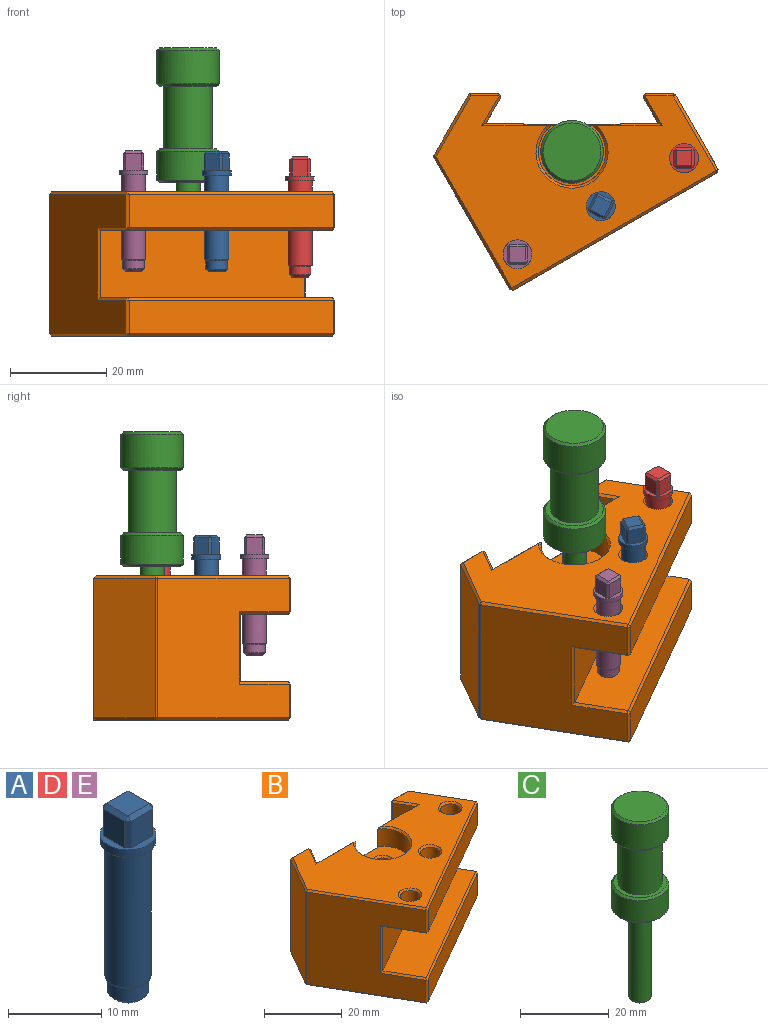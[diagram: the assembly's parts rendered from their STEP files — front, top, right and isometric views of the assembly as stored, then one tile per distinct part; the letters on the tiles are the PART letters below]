
ASSEMBLY  parts=5 mates=4
PART A: 25 faces, bbox 6x6x25 mm
  f0: cylinder r=3mm len=6mm, axis (0,0,-1), area 18.8mm2, adj f3,f5
  f1: cylinder r=2.25mm len=4.5mm, axis (0,0,-1), area 24.7mm2, adj f23,f24
  f2: plane 3.5x3.5mm, normal (0,0,-1), area 9.6mm2, adj f23
  f3: plane 6x6mm, normal (0,0,-1), area 8.6mm2, adj f0,f4
  f4: cylinder r=2.5mm len=17.5mm, axis (0,0,-1), area 274.9mm2, adj f3,f24
  f5: plane 6x6mm, normal (0,0,1), area 10.8mm2, adj f0,f6,f7,f8,f9,f11,f13,f16
  f6: plane 3.5x3.24mm, normal (0,1,0), area 11.3mm2, adj f5,f13,f19,f22
  f7: plane 3.5x3.24mm, normal (1,0,0), area 11.3mm2, adj f5,f11,f13,f14
  f8: plane 3.5x3.24mm, normal (0,-1,0), area 11.3mm2, adj f5,f11,f15,f16
  f9: plane 3.5x3.24mm, normal (-1,0,0), area 11.3mm2, adj f5,f16,f20,f22
  f10: plane 3.24x3.24mm, normal (0,0,1), area 10.5mm2, adj f14,f15,f19,f20
  f11: plane 3.5x0.5mm, normal (0.71,-0.71,0), area 2.5mm2, adj f5,f7,f8,f12
  f12: plane 0.5x0.5mm, normal (0.58,-0.58,0.58), area 0.2mm2, adj f11,f14,f15
  f13: plane 3.5x0.5mm, normal (0.71,0.71,0), area 2.5mm2, adj f5,f6,f7,f17
  f14: plane 3.24x0.5mm, normal (0.71,0,0.71), area 2.3mm2, adj f7,f10,f12,f17
  f15: plane 3.24x0.5mm, normal (0,-0.71,0.71), area 2.3mm2, adj f8,f10,f12,f18
  f16: plane 3.5x0.5mm, normal (-0.71,-0.71,0), area 2.5mm2, adj f5,f8,f9,f18
  f17: plane 0.5x0.5mm, normal (0.58,0.58,0.58), area 0.2mm2, adj f13,f14,f19
  f18: plane 0.5x0.5mm, normal (-0.58,-0.58,0.58), area 0.2mm2, adj f15,f16,f20
  f19: plane 3.24x0.5mm, normal (0,0.71,0.71), area 2.3mm2, adj f6,f10,f17,f21
  f20: plane 3.24x0.5mm, normal (-0.71,0,0.71), area 2.3mm2, adj f9,f10,f18,f21
  f21: plane 0.5x0.5mm, normal (-0.58,0.58,0.58), area 0.2mm2, adj f19,f20,f22
  f22: plane 3.5x0.5mm, normal (-0.71,0.71,0), area 2.5mm2, adj f5,f6,f9,f21
  f23: cone r=1.75mm half-angle=45deg, axis (0,0,1), area 8.9mm2, adj f1,f2
  f24: cone r=2mm half-angle=45deg, axis (0,0,1), area 5.3mm2, adj f1,f4
PART B: 83 faces, bbox 59.1x40.9x30 mm
  f0: plane 29x7.91mm, normal (0,1,0), area 229.4mm2, adj f3,f4,f13,f80
  f1: cylinder r=7mm len=14mm, axis (0,0,1), area 196.3mm2, adj f2,f5,f21,f82
  f2: cone r=7mm half-angle=45deg, axis (0,0,1), area 25.4mm2, adj f1,f3,f19,f38,f82
  f3: plane 14.51x0.5mm, normal (0,0.71,0.71), area 8.2mm2, adj f0,f2,f19,f56,f80,f82
  f4: plane 37.56x0.5mm, normal (0,0.71,-0.71), area 20.3mm2, adj f0,f10,f20,f55,f65,f80,f81,f82
  f5: plane 8.67x0.31mm, normal (0,0.71,0.71), area 3.5mm2, adj f1,f21,f82
  f6: plane 42.44x24.5mm, normal (0.5,-0.87,0), area 343mm2, adj f31,f32,f45,f46
  f7: cylinder r=2.5mm len=7mm, axis (0,0,1), area 110mm2, adj f73,f74
  f8: cylinder r=2.5mm len=7mm, axis (0,0,1), area 110mm2, adj f75,f76
  f9: cylinder r=2.5mm len=7mm, axis (0,0,1), area 110mm2, adj f77,f78
  f10: plane 29x7.91mm, normal (0,1,0), area 229.4mm2, adj f4,f12,f38,f81
  f11: plane 29.5x5.81mm, normal (0,1,0), area 171.3mm2, adj f20,f36,f43,f50,f51
  f12: plane 29x5.4mm, normal (-0.87,-0.5,0), area 180.8mm2, adj f10,f37,f51,f55
  f13: plane 29x5.4mm, normal (0.87,-0.5,0), area 180.8mm2, adj f0,f56,f65,f66
  f14: plane 29x6.12mm, normal (0,1,0), area 177.3mm2, adj f15,f57,f66,f71
  f15: plane 29x12.8mm, normal (-0.87,0.5,0), area 428.6mm2, adj f14,f58,f67,f72
  f16: plane 29x27.39mm, normal (-0.87,-0.5,0), area 737.3mm2, adj f33,f41,f46,f47,f59,f60,f67,f68
  f17: plane 42.44x24.5mm, normal (0.5,-0.87,0), area 343mm2, adj f48,f49,f60,f61
  f18: plane 29x15.44mm, normal (0.87,0.5,0), area 337.1mm2, adj f27,f29,f30,f31,f34,f43,f49,f50
  f19: plane 58.25x39.94mm, normal (0,0,1), area 1019.3mm2, adj f2,f3,f30,f36,f37,f38,f45,f56
  f20: plane 58.25x40.44mm, normal (0,0,-1), area 1269.7mm2, adj f4,f11,f50,f51,f55,f61,f65,f68
  f21: plane 14x12.5mm, normal (0,0,1), area 116.8mm2, adj f1,f5,f79
  f22: plane 5x5mm, normal (0,0,1), area 19.6mm2, adj f23
  f23: cylinder r=2.5mm len=9.5mm, axis (0,0,1), area 149.2mm2, adj f22,f79
  f24: plane 48.19x34.46mm, normal (0,0,-1), area 478.7mm2, adj f26,f27,f32,f33,f73,f76,f77
  f25: plane 48.19x34.46mm, normal (0,0,1), area 563.5mm2, adj f26,f34,f47,f48
  f26: plane 42.44x24.5mm, normal (0.5,-0.87,0), area 686mm2, adj f24,f25,f29,f41
  f27: plane 10.64x6.18mm, normal (0.61,0.35,-0.71), area 8.3mm2, adj f18,f24,f28,f29
  f28: plane 0.68x0.5mm, normal (0.79,-0.21,-0.58), area 0.2mm2, adj f27,f31,f32
  f29: plane 15x0.68mm, normal (0.97,-0.26,0), area 10.3mm2, adj f18,f26,f27,f34
  f30: plane 15.69x9.35mm, normal (0.61,0.35,0.71), area 12.6mm2, adj f18,f19,f35,f39
  f31: plane 7x0.68mm, normal (0.97,-0.26,0), area 4.9mm2, adj f6,f18,f28,f39
  f32: plane 42.69x24.93mm, normal (0.35,-0.61,-0.71), area 34.6mm2, adj f6,f24,f28,f40
  f33: plane 10.39x6.43mm, normal (-0.61,-0.35,-0.71), area 8.3mm2, adj f16,f24,f40,f41
  f34: plane 10.64x6.18mm, normal (0.61,0.35,0.71), area 8.3mm2, adj f18,f25,f29,f42
  f35: plane 0.5x0.5mm, normal (0.38,0.65,0.65), area 0.2mm2, adj f30,f36,f43
  f36: plane 5.81x0.5mm, normal (0,0.71,0.71), area 4.1mm2, adj f11,f19,f35,f44
  f37: plane 6.15x3.98mm, normal (-0.61,-0.35,0.71), area 4.7mm2, adj f12,f19,f38,f44
  f38: plane 14.51x0.5mm, normal (0,0.71,0.71), area 8.2mm2, adj f2,f10,f19,f37,f81,f82
  f39: plane 0.68x0.5mm, normal (0.79,-0.21,0.58), area 0.2mm2, adj f30,f31,f45
  f40: plane 0.68x0.5mm, normal (-0.21,-0.79,-0.58), area 0.2mm2, adj f32,f33,f46
  f41: plane 15x0.68mm, normal (-0.26,-0.97,0), area 10.3mm2, adj f16,f26,f33,f47
  f42: plane 0.68x0.5mm, normal (0.79,-0.21,0.58), area 0.2mm2, adj f34,f48,f49
  f43: plane 29.25x0.43mm, normal (0.5,0.87,0), area 14.6mm2, adj f11,f18,f35,f50
  f44: plane 0.75x0.5mm, normal (-0.77,0.45,0.45), area 0.2mm2, adj f36,f37,f51
  f45: plane 42.69x24.93mm, normal (0.35,-0.61,0.71), area 34.6mm2, adj f6,f19,f39,f52
  f46: plane 7x0.68mm, normal (-0.26,-0.97,0), area 4.9mm2, adj f6,f16,f40,f52
  f47: plane 10.39x6.43mm, normal (-0.61,-0.35,0.71), area 8.3mm2, adj f16,f25,f41,f53
  f48: plane 42.69x24.93mm, normal (0.35,-0.61,0.71), area 34.6mm2, adj f17,f25,f42,f53
  f49: plane 7x0.68mm, normal (0.97,-0.26,0), area 4.9mm2, adj f17,f18,f42,f54
  f50: plane 15.94x9.64mm, normal (0.61,0.35,-0.71), area 12.9mm2, adj f11,f18,f20,f43,f54
  f51: plane 29.5x0.75mm, normal (-0.87,0.5,0), area 25.4mm2, adj f11,f12,f20,f44,f55
  f52: plane 0.68x0.5mm, normal (-0.21,-0.79,0.58), area 0.2mm2, adj f45,f46,f59
  f53: plane 0.68x0.5mm, normal (-0.21,-0.79,0.58), area 0.2mm2, adj f47,f48,f60
  f54: plane 0.68x0.5mm, normal (0.79,-0.21,-0.58), area 0.2mm2, adj f49,f50,f61
  f55: plane 6.4x3.98mm, normal (-0.61,-0.35,-0.71), area 4.8mm2, adj f4,f12,f20,f51
  f56: plane 6.15x3.98mm, normal (0.61,-0.35,0.71), area 4.7mm2, adj f3,f13,f19,f62
  f57: plane 6.12x0.5mm, normal (0,0.71,0.71), area 4.2mm2, adj f14,f19,f58,f62
  f58: plane 13.05x7.68mm, normal (-0.61,0.35,0.71), area 10.3mm2, adj f15,f19,f57,f63
  f59: plane 27.64x16.25mm, normal (-0.61,-0.35,0.71), area 22.4mm2, adj f16,f19,f52,f63
  f60: plane 7x0.68mm, normal (-0.26,-0.97,0), area 4.9mm2, adj f16,f17,f53,f64
  f61: plane 42.69x24.93mm, normal (0.35,-0.61,-0.71), area 34.6mm2, adj f17,f20,f54,f64
  f62: plane 0.75x0.5mm, normal (0.77,0.45,0.45), area 0.2mm2, adj f56,f57,f66
  f63: plane 0.5x0.5mm, normal (-0.76,0,0.65), area 0.2mm2, adj f58,f59,f67
  f64: plane 0.68x0.5mm, normal (-0.21,-0.79,-0.58), area 0.2mm2, adj f60,f61,f68
  f65: plane 6.15x3.98mm, normal (0.61,-0.35,-0.71), area 4.7mm2, adj f4,f13,f20,f69
  f66: plane 29x0.75mm, normal (0.87,0.5,0), area 25.1mm2, adj f13,f14,f62,f69
  f67: plane 29x0.5mm, normal (-1,0,0), area 14.5mm2, adj f15,f16,f63,f70
  f68: plane 27.64x16.25mm, normal (-0.61,-0.35,-0.71), area 22.4mm2, adj f16,f20,f64,f70
  f69: plane 0.75x0.5mm, normal (0.77,0.45,-0.45), area 0.2mm2, adj f65,f66,f71
  f70: plane 0.5x0.5mm, normal (-0.76,0,-0.65), area 0.2mm2, adj f67,f68,f72
  f71: plane 6.12x0.5mm, normal (0,0.71,-0.71), area 4.2mm2, adj f14,f20,f69,f72
  f72: plane 13.05x7.68mm, normal (-0.61,0.35,-0.71), area 10.3mm2, adj f15,f20,f70,f71
  f73: cone r=3mm half-angle=45deg, axis (0,0,-1), area 12.2mm2, adj f7,f24
  f74: cone r=2.5mm half-angle=45deg, axis (0,0,1), area 12.2mm2, adj f7,f19
  f75: cone r=2.5mm half-angle=45deg, axis (0,0,1), area 12.2mm2, adj f8,f19
  f76: cone r=3mm half-angle=45deg, axis (0,0,-1), area 12.2mm2, adj f8,f24
  f77: cone r=3mm half-angle=45deg, axis (0,0,-1), area 12.2mm2, adj f9,f24
  f78: cone r=2.5mm half-angle=45deg, axis (0,0,1), area 12.2mm2, adj f9,f19
  f79: cone r=2.5mm half-angle=45deg, axis (0,0,1), area 12.2mm2, adj f21,f23
  f80: plane 29.4x0.2mm, normal (1,0,0), area 5.8mm2, adj f0,f3,f4,f82
  f81: plane 29.4x0.2mm, normal (-1,0,0), area 5.8mm2, adj f4,f10,f38,f82
  f82: plane 29.41x20.01mm, normal (0,1,0), area 540.9mm2, adj f1,f2,f3,f4,f5,f38,f80,f81
PART C: 14 faces, bbox 13x13x53 mm
  f0: plane 12x12mm, normal (0,0,1), area 113.1mm2, adj f13
  f1: cylinder r=6.5mm len=13mm, axis (0,0,1), area 285.9mm2, adj f12,f13
  f2: plane 12x12mm, normal (0,0,-1), area 34.6mm2, adj f3,f12
  f3: cylinder r=5mm len=13mm, axis (0,0,1), area 408.4mm2, adj f2,f4
  f4: plane 12x12mm, normal (0,0,1), area 34.6mm2, adj f3,f11
  f5: cylinder r=6.5mm len=13mm, axis (0,0,1), area 245mm2, adj f10,f11
  f6: plane 12x12mm, normal (0,0,-1), area 93.5mm2, adj f7,f10
  f7: cylinder r=2.5mm len=24.5mm, axis (0,0,1), area 384.8mm2, adj f6,f9
  f8: plane 4x4mm, normal (0,0,-1), area 12.6mm2, adj f9
  f9: cone r=2.5mm half-angle=45deg, axis (0,0,1), area 10mm2, adj f7,f8
  f10: cone r=6.5mm half-angle=45deg, axis (0,0,1), area 27.8mm2, adj f5,f6
  f11: cone r=6mm half-angle=45deg, axis (0,0,-1), area 27.8mm2, adj f4,f5
  f12: cone r=6.5mm half-angle=45deg, axis (0,0,1), area 27.8mm2, adj f1,f2
  f13: cone r=6mm half-angle=45deg, axis (0,0,-1), area 27.8mm2, adj f0,f1
PART D: same geometry as A
PART E: same geometry as A
PLACE A rot(axis=(0,0,1),153.2deg) t=(18.47,17.01,16.98)mm
PLACE B t=(-12.53,10.56,0)mm
PLACE C rot(axis=(0,0,-1),165.8deg) t=(12.48,28.29,31.92)mm
PLACE D t=(35.79,27.01,15.83)mm
PLACE E t=(1.15,7.01,17.08)mm
MATE cylindrical A.f0 <-> B.f8  axis (0,0,-1) through (18.47,17.01,24.65)mm
MATE cylindrical C.f1 <-> B.f1  axis (0,0,1) through (12.48,28.29,19.67)mm
MATE cylindrical D.f0 <-> B.f9  axis (0,0,-1) through (35.79,27.01,23.5)mm
MATE cylindrical E.f0 <-> B.f7  axis (0,0,-1) through (1.15,7.01,16)mm
